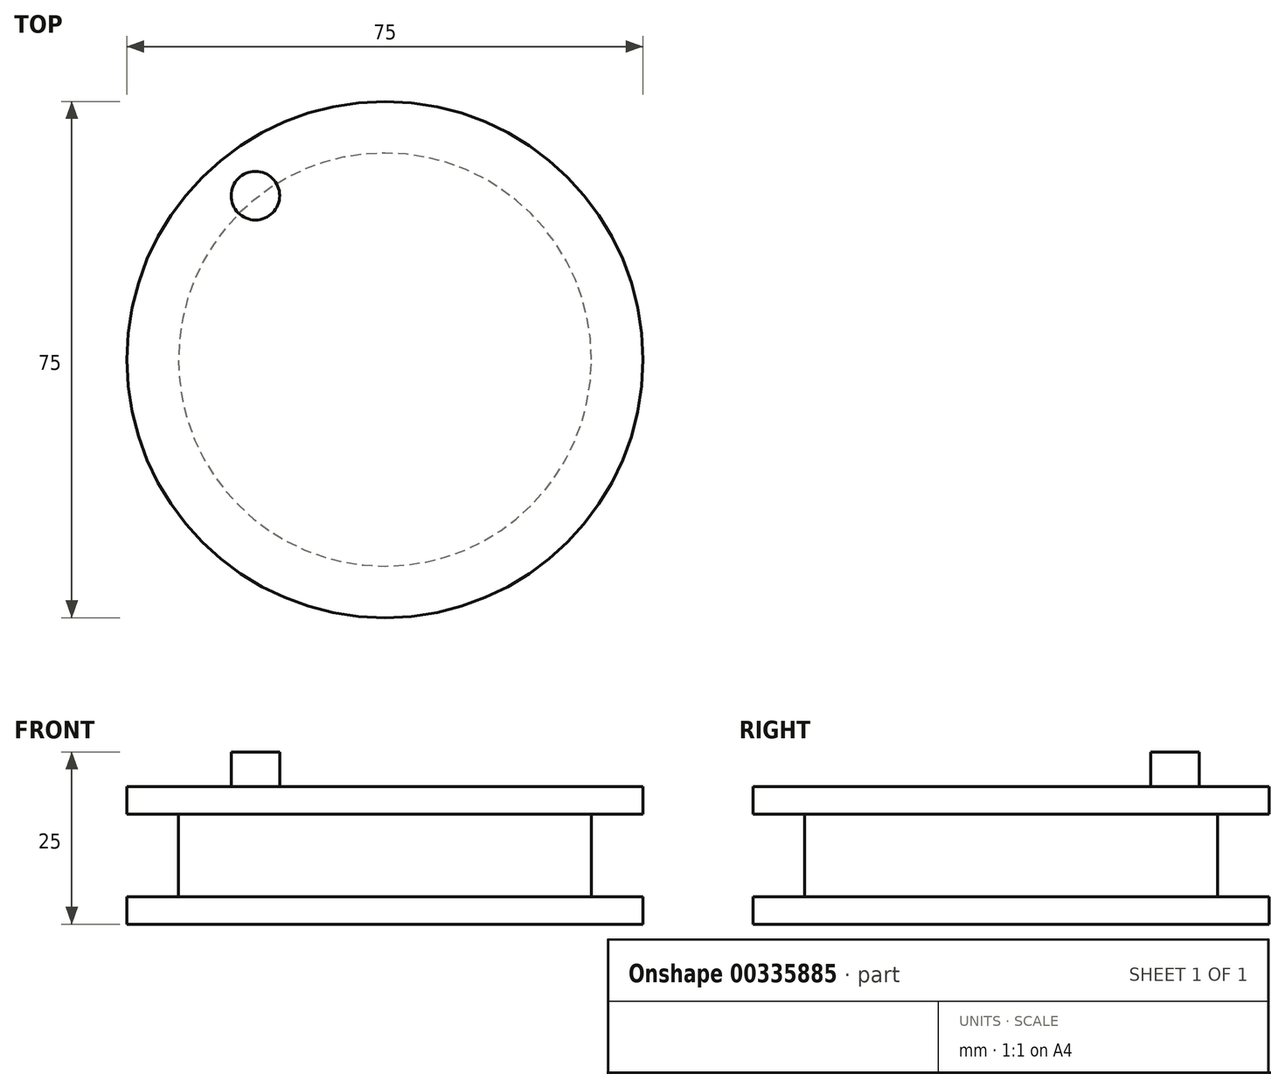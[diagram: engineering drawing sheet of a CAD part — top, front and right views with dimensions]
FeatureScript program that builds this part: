
annotation { "Feature Type Name" : "Feature", "Feature Type Description" : "" }
export const myFeature = defineFeature(function(context is Context, id is Id, definition is map)
    precondition{}
    {
        {
            assignVariable(context, id + "F0", {"name" : "alt_flange", "anyValue" : 4});
        }
        {
            assignVariable(context, id + "F1", {"name" : "alt_cinghia", "anyValue" : 12});
        }
        {
            var Q0;
            Q0=qCreatedBy(makeId("Top.planeOp"),FACE);
            var sketch = newSketch(context, id + "F2", { "sketchPlane" : qUnion([Q0])});
            skCircle(sketch, "E0", {"center": v(0, 0) * mm, "radius": 37.5 * mm});
            skSolve(sketch);
        }
        {
            var Q0;
            Q0=qSketchRegion(id+"F2",true);
            extrude(context, id + "F3", {"entities" : qUnion([Q0]), "depth" : (getVariable(context, 'alt_flange')) * mm});
        }
        {
            var Q0;
            Q0=qCreatedBy(makeId("Top.planeOp"),FACE);
            cPlane(context, id + "F4", {"entities" : qUnion([Q0]), "cplaneType" : CPlaneType.OFFSET, "offset" : (getVariable(context, 'alt_flange')) * mm, "width" : 150 * mm, "height" : 150 * mm});
        }
        {
            var Q0;
            Q0=qCreatedBy(id+"F4.planeOp",FACE);
            var sketch = newSketch(context, id + "F5", { "sketchPlane" : qUnion([Q0])});
            skCircle(sketch, "E1", {"center": v(0, 0) * mm, "radius": 30 * mm});
            skSolve(sketch);
        }
        {
            var Q0;
            Q0=qSketchRegion(id+"F5",true);
            extrude(context, id + "F6", {"entities" : qUnion([Q0]), "operationType" : NewBodyOperationType.ADD, "depth" : (getVariable(context, 'alt_cinghia')) * mm});
        }
        {
            var Q0;
            Q0=qCreatedBy(id+"F4.planeOp",FACE);
            cPlane(context, id + "F7", {"entities" : qUnion([Q0]), "cplaneType" : CPlaneType.OFFSET, "offset" : (getVariable(context, 'alt_cinghia')) * mm, "width" : 150 * mm, "height" : 150 * mm});
        }
        {
            var Q0;
            Q0=qCreatedBy(id+"F7.planeOp",FACE);
            var sketch = newSketch(context, id + "F8", { "sketchPlane" : qUnion([Q0])});
            skCircle(sketch, "E2", {"center": v(0, 0) * mm, "radius": 37.5 * mm});
            skSolve(sketch);
        }
        {
            var Q0;
            Q0=qSketchRegion(id+"F8",true);
            extrude(context, id + "F9", {"entities" : qUnion([Q0]), "operationType" : NewBodyOperationType.ADD, "depth" : (getVariable(context, 'alt_flange')) * mm});
        }
        {
            var Q0;
            Q0=makeQuery(id+"F3.opExtrude","SWEPT_BODY",BODY,{"disambiguationData":[OSD([sQuery(id+"F2.wireOp",EDGE,"E0")])]});
            transform(context, id + "F10", {"entities" : qUnion([Q0]), "transformType" : TransformType.TRANSLATION_3D, "dx" : 0 * mm, "dy" : 0 * mm, "dz" : (getVariable(context, 'alt_flange') * 2 + getVariable(context, 'alt_cinghia')) * mm, "makeCopy" : true});
        }
        {
            var Q0;
            Q0=makeQuery(id+"F10.opPattern","COPY",BODY,{"derivedFrom":makeQuery(id+"F3.opExtrude","SWEPT_BODY",BODY,{"disambiguationData":[OSD([sQuery(id+"F2.wireOp",EDGE,"E0")])]}),"instanceName":"1"});
            deleteBodies(context, id + "F11", {"entities" : qUnion([Q0])});
        }
        {
            var Q0;
            Q0=makeQuery(id+"F3.opExtrude","SWEPT_BODY",BODY,{"disambiguationData":[OSD([sQuery(id+"F2.wireOp",EDGE,"E0")])]});
            transform(context, id + "F12", {"entities" : qUnion([Q0]), "transformType" : TransformType.COPY});
        }
        {
            var Q0;
            Q0=makeQuery(id+"F12.opPattern","COPY",BODY,{"derivedFrom":makeQuery(id+"F3.opExtrude","SWEPT_BODY",BODY,{"disambiguationData":[OSD([sQuery(id+"F2.wireOp",EDGE,"E0")])]}),"instanceName":"1"});
            deleteBodies(context, id + "F13", {"entities" : qUnion([Q0])});
        }
        {
            var Q0;
            Q0=makeQuery(id+"F3.opExtrude","SWEPT_BODY",BODY,{"disambiguationData":[OSD([sQuery(id+"F2.wireOp",EDGE,"E0")])]});
            transform(context, id + "F14", {"entities" : qUnion([Q0]), "transformType" : TransformType.TRANSLATION_3D, "dx" : 0 * mm, "dy" : 0 * mm, "dz" : (2 * (getVariable(context, 'alt_flange') * 2 + getVariable(context, 'alt_cinghia'))) * mm, "makeCopy" : false});
        }
        {
            var Q0;
            Q0=makeQuery(id+"F9.opExtrude","CAP_FACE",FACE,{"disambiguationData":[OSD([sQuery(id+"F8.wireOp",EDGE,"E2")])],"isStart":false});
            var sketch = newSketch(context, id + "F15", { "sketchPlane" : qUnion([Q0])});
            skCircle(sketch, "E3", {"center": v(-18.83, 23.81) * mm, "radius": 3.53 * mm});
            skSolve(sketch);
        }
        {
            var Q0;
            Q0 = qSketchRegion(id + "F15", true);
            extrude(context, id + "F16", {"entities" : qUnion([Q0]), "operationType" : NewBodyOperationType.ADD, "depth" : 5 * mm});
        }
    });
